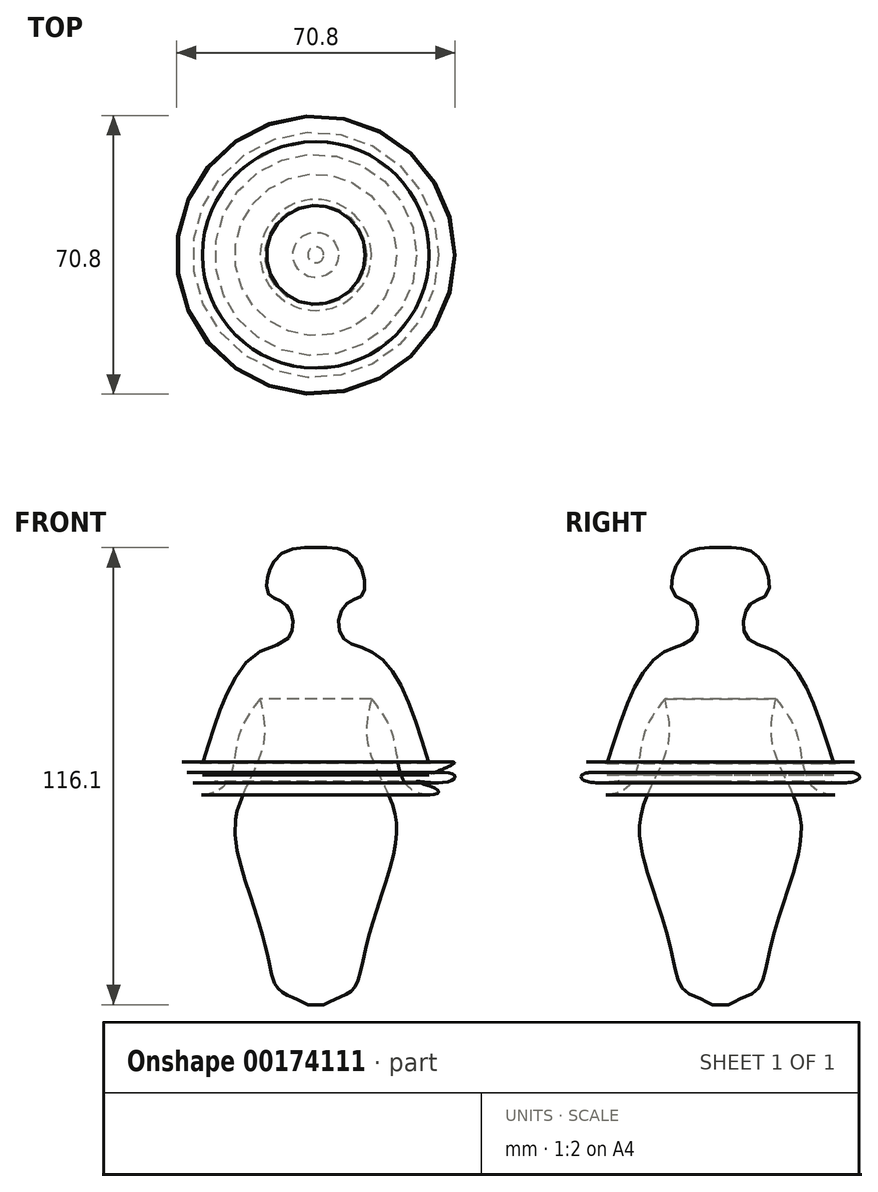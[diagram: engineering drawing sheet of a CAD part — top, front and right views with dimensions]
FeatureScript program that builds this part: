
annotation { "Feature Type Name" : "Feature", "Feature Type Description" : "" }
export const myFeature = defineFeature(function(context is Context, id is Id, definition is map)
    precondition{}
    {
        {
            var Q0;
            Q0=qCreatedBy(makeId("Front.planeOp"),FACE);
            var sketch = newSketch(context, id + "F0", { "sketchPlane" : qUnion([Q0])});
            skFitSpline(sketch, "E0", {"points": [v(0, 41.16) * mm, v(9.5, 39.14) * mm, v(12.09, 29.64) * mm, v(7.48, 26.77) * mm, v(6.62, 18.7) * mm, v(15.83, 13.81) * mm, v(28.78, -13.53) * mm], "startDerivative": vector(68.58, 3.67) * mm, "endDerivative": vector(39.32, -127.1) * mm});
            skFitSpline(sketch, "E1", {"points": [v(14.1, 2.88) * mm, v(13.24, -8.64) * mm, v(19, -22.74) * mm, v(20.15, -34.83) * mm, v(13.24, -58.14) * mm, v(9.79, -70.52) * mm, v(6.33, -72.82) * mm, v(2.01, -74.84) * mm], "startDerivative": vector(-17.36, -77.6) * mm, "endDerivative": vector(-47.17, -22.8) * mm});
            skFitSpline(sketch, "E2", {"points": [v(14.1, 2.88) * mm, v(19.57, -6.62) * mm, v(23.31, -19.29) * mm, v(30.5, -21.3) * mm, v(31.08, -20.44) * mm, v(25.61, -18.14) * mm, v(32.23, -18.42) * mm, v(35.4, -16.98) * mm, v(32.8, -15.83) * mm, v(28.78, -16.4) * mm, v(35.11, -13.53) * mm, v(28.78, -13.53) * mm], "startDerivative": vector(52.43, -66.95) * mm, "endDerivative": vector(-110.04, -11.08) * mm});
            skLineSegment(sketch, "E3", {"start": v(2.01, -74.84) * mm, "end": v(0, -74.84) * mm});
            skLineSegment(sketch, "E4", {"start": v(0, 41.16) * mm, "end": v(0, -74.84) * mm});
            skSolve(sketch);
        }
        {
            var Q0;
            Q0 = qSketchRegion(id + "F0", true);
            var Q1;
            Q1=sQuery(id+"F0.wireOp",EDGE,"E4");
            revolve(context, id + "F1", {"entities" : qUnion([Q0]), "axis" : qUnion([Q1]), "revolveType" : RevolveType.FULL});
        }
    });
